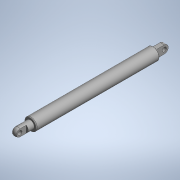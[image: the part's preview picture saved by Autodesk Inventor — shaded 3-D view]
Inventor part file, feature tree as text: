
AUTODESK INVENTOR PART (.ipt)
format: ipt  version: 2020 (Build 240168000, 168)  size: 103,936 bytes
history: native  units: mm (DEFAULTED — no unit token found)
features: other x1, extrude x1
ambient origin geometry x8: Origin, YZ Plane, XZ Plane, XY Plane, X Axis, Y Axis, Z Axis, Center Point
bodies: Solid1 (feature_tree), Solid2 (feature_tree)
feature tree (2):
  other  "LPattern1"
  extrude  "Extrude2"  [1 undecoded]
note: 1 required parameter value undecoded (feature->parameter linkage not recoverable at this tier; creation-order binding heuristic only, values carry confidence <= 0.55)
